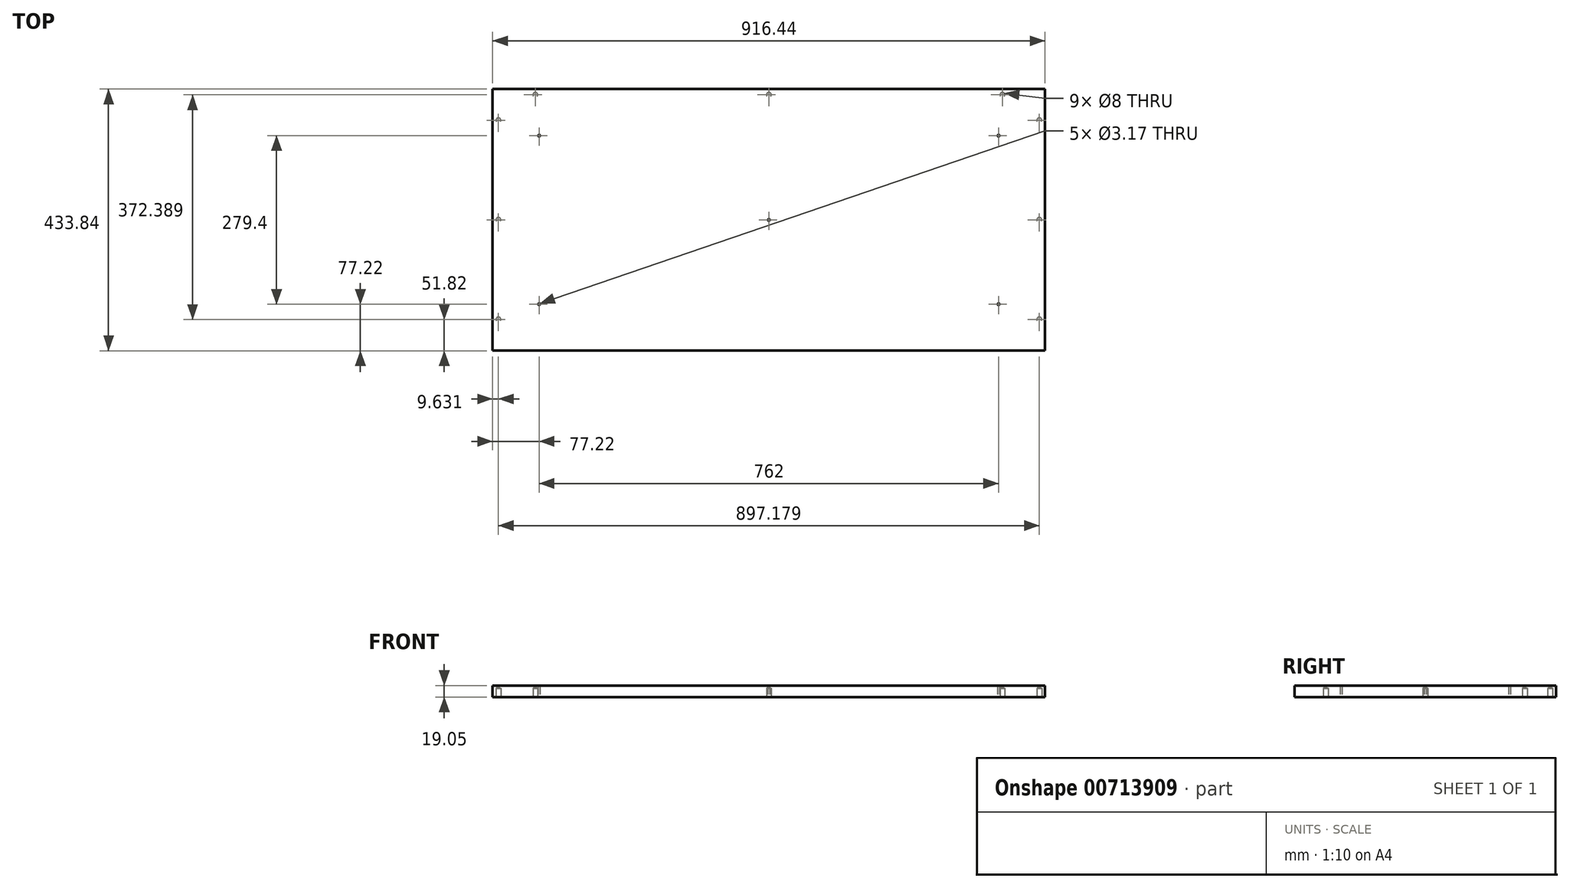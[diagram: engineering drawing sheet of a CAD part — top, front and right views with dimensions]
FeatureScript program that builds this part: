
annotation { "Feature Type Name" : "Feature", "Feature Type Description" : "" }
export const myFeature = defineFeature(function(context is Context, id is Id, definition is map)
    precondition{}
    {
        {
            var Q0;
            Q0=qCreatedBy(makeId("Top.planeOp"),FACE);
            var sketch = newSketch(context, id + "F0", { "sketchPlane" : qUnion([Q0])});
            skLineSegment(sketch, "E0.bottom", {"start": v(458.22, 216.92) * mm, "end": v(-458.22, 216.92) * mm});
            skLineSegment(sketch, "E0.top", {"start": v(458.22, -216.92) * mm, "end": v(-458.22, -216.92) * mm});
            skLineSegment(sketch, "E0.left", {"start": v(458.22, 216.92) * mm, "end": v(458.22, -216.92) * mm});
            skLineSegment(sketch, "E0.right", {"start": v(-458.22, 216.92) * mm, "end": v(-458.22, -216.92) * mm});
            skPoint(sketch, "E0.middle", {"position": v(0, 0) * mm});
            skSolve(sketch);
        }
        {
            var Q0;
            Q0=makeQuery(id+"F0.imprint","IMPRINT",FACE,{"disambiguationData":[TD([[makeQuery(id+"F0.imprint","IMPRINT",EDGE,{"derivedFrom":sQuery(id+"F0.wireOp",EDGE,"E0.bottom")}),1.0]])]});
            extrude(context, id + "F1", {"entities" : qUnion([Q0]), "depth" : 19.05 * mm, "offsetDistance" : 25.4 * mm});
        }
        {
            var Q0;
            Q0=makeQuery(id+"F1.opExtrude","CAP_FACE",FACE,{"disambiguationData":[OSD([sQuery(id+"F0.wireOp",EDGE,"E0.bottom"),sQuery(id+"F0.wireOp",EDGE,"E0.top"),sQuery(id+"F0.wireOp",EDGE,"E0.left"),sQuery(id+"F0.wireOp",EDGE,"E0.right")])],"isStart":true});
            var sketch = newSketch(context, id + "F2", { "sketchPlane" : qUnion([Q0])});
            skLineSegment(sketch, "E1", {"start": v(-458.22, 216.92) * mm, "end": v(-448.59, 216.92) * mm});
            skLineSegment(sketch, "E2", {"start": v(-448.59, 216.92) * mm, "end": v(-448.59, -216.92) * mm});
            skLineSegment(sketch, "E3", {"start": v(458.22, 216.92) * mm, "end": v(448.59, 216.92) * mm});
            skLineSegment(sketch, "E4", {"start": v(448.59, 216.92) * mm, "end": v(448.59, -216.92) * mm});
            skLineSegment(sketch, "E5", {"start": v(-448.59, -216.92) * mm, "end": v(-448.59, -207.29) * mm});
            skLineSegment(sketch, "E6", {"start": v(-448.59, -207.29) * mm, "end": v(448.59, -207.29) * mm});
            skLineSegment(sketch, "E7", {"start": v(448.59, -207.29) * mm, "end": v(458.22, -207.29) * mm});
            skLineSegment(sketch, "E8", {"start": v(-448.59, -207.29) * mm, "end": v(-458.22, -207.29) * mm});
            skLineSegment(sketch, "E9", {"start": v(-458.22, -207.29) * mm, "end": v(-387.35, -207.29) * mm});
            skLineSegment(sketch, "E10", {"start": v(458.22, -207.29) * mm, "end": v(387.35, -207.29) * mm});
            skLineSegment(sketch, "E11", {"start": v(0, -216.92) * mm, "end": v(0, -207.29) * mm});
            skLineSegment(sketch, "E12", {"start": v(-448.59, 216.92) * mm, "end": v(-448.59, 165.1) * mm});
            skLineSegment(sketch, "E13", {"start": v(448.59, 216.92) * mm, "end": v(448.59, 165.1) * mm});
            skLineSegment(sketch, "E14", {"start": v(-448.59, -216.92) * mm, "end": v(-448.59, -165.1) * mm});
            skLineSegment(sketch, "E15", {"start": v(448.59, -216.92) * mm, "end": v(448.59, -165.1) * mm});
            skLineSegment(sketch, "E16", {"start": v(-458.22, 0) * mm, "end": v(-448.59, 0) * mm});
            skLineSegment(sketch, "E17", {"start": v(458.22, 0) * mm, "end": v(448.59, 0) * mm});
            skPoint(sketch, "E18", {"position": v(-448.59, 165.1) * mm});
            skPoint(sketch, "E19", {"position": v(-448.59, 0) * mm});
            skPoint(sketch, "E20", {"position": v(-448.59, -165.1) * mm});
            skPoint(sketch, "E21", {"position": v(-387.35, -207.29) * mm});
            skPoint(sketch, "E22", {"position": v(0, -207.29) * mm});
            skPoint(sketch, "E23", {"position": v(387.35, -207.29) * mm});
            skPoint(sketch, "E24", {"position": v(448.59, -165.1) * mm});
            skPoint(sketch, "E25", {"position": v(448.59, 0) * mm});
            skPoint(sketch, "E26", {"position": v(448.59, 165.1) * mm});
            skSolve(sketch);
        }
        {
            var Q0;
            Q0=sQuery(id+"F2.wireOp",VERTEX,"E18");
            var Q1;
            Q1=sQuery(id+"F2.wireOp",VERTEX,"E19");
            var Q2;
            Q2=sQuery(id+"F2.wireOp",VERTEX,"E20");
            var Q3;
            Q3=sQuery(id+"F2.wireOp",VERTEX,"E21");
            var Q4;
            Q4=sQuery(id+"F2.wireOp",VERTEX,"E22");
            var Q5;
            Q5=sQuery(id+"F2.wireOp",VERTEX,"E23");
            var Q6;
            Q6=sQuery(id+"F2.wireOp",VERTEX,"E24");
            var Q7;
            Q7=sQuery(id+"F2.wireOp",VERTEX,"E25");
            var Q8;
            Q8=sQuery(id+"F2.wireOp",VERTEX,"E26");
            var Q9;
            Q9=makeQuery(id+"F1.opExtrude","SWEPT_BODY",BODY,{"disambiguationData":[OSD([sQuery(id+"F0.wireOp",EDGE,"E0.bottom"),sQuery(id+"F0.wireOp",EDGE,"E0.top"),sQuery(id+"F0.wireOp",EDGE,"E0.left"),sQuery(id+"F0.wireOp",EDGE,"E0.right")])]});
            hole(context, id + "F3", {"style" : HoleStyle.SIMPLE, "endStyle" : HoleEndStyle.BLIND, "holeDiameter" : 8 * mm, "majorDiameter" : 6.35 * mm, "holeDepth" : 14.22 * mm, "isTappedThrough" : true, "tappedDepth" : 12.7 * mm, "tapClearance" : 3, "startFromSketch" : true, "locations" : qUnion([Q0, Q1, Q2, Q3, Q4, Q5, Q6, Q7, Q8]), "scope" : qUnion([Q9])});
        }
        {
            var Q0;
            Q0=makeQuery(id+"F1.opExtrude","CAP_FACE",FACE,{"disambiguationData":[OSD([sQuery(id+"F0.wireOp",EDGE,"E0.bottom"),sQuery(id+"F0.wireOp",EDGE,"E0.top"),sQuery(id+"F0.wireOp",EDGE,"E0.left"),sQuery(id+"F0.wireOp",EDGE,"E0.right")])],"isStart":true});
            var sketch = newSketch(context, id + "F4", { "sketchPlane" : qUnion([Q0])});
            skLineSegment(sketch, "E27.bottom", {"start": v(381, 139.7) * mm, "end": v(-381, 139.7) * mm});
            skLineSegment(sketch, "E27.top", {"start": v(381, -139.7) * mm, "end": v(-381, -139.7) * mm});
            skLineSegment(sketch, "E27.left", {"start": v(381, 139.7) * mm, "end": v(381, -139.7) * mm});
            skLineSegment(sketch, "E27.right", {"start": v(-381, 139.7) * mm, "end": v(-381, -139.7) * mm});
            skPoint(sketch, "E27.middle", {"position": v(0, 0) * mm});
            skPoint(sketch, "E28", {"position": v(-381, 139.7) * mm});
            skPoint(sketch, "E29", {"position": v(-381, -139.7) * mm});
            skPoint(sketch, "E30", {"position": v(381, 139.7) * mm});
            skPoint(sketch, "E31", {"position": v(381, -139.7) * mm});
            skSolve(sketch);
        }
        {
            var Q0;
            Q0=sQuery(id+"F4.wireOp",VERTEX,"E28");
            var Q1;
            Q1=sQuery(id+"F4.wireOp",VERTEX,"E27.middle");
            var Q2;
            Q2=sQuery(id+"F4.wireOp",VERTEX,"E29");
            var Q3;
            Q3=sQuery(id+"F4.wireOp",VERTEX,"E31");
            var Q4;
            Q4=sQuery(id+"F4.wireOp",VERTEX,"E30");
            var Q5;
            Q5=makeQuery(id+"F1.opExtrude","SWEPT_BODY",BODY,{"disambiguationData":[OSD([sQuery(id+"F0.wireOp",EDGE,"E0.bottom"),sQuery(id+"F0.wireOp",EDGE,"E0.top"),sQuery(id+"F0.wireOp",EDGE,"E0.left"),sQuery(id+"F0.wireOp",EDGE,"E0.right")])]});
            hole(context, id + "F5", {"style" : HoleStyle.SIMPLE, "endStyle" : HoleEndStyle.BLIND, "holeDiameter" : 3.17 * mm, "majorDiameter" : 6.35 * mm, "holeDepth" : 20.32 * mm, "isTappedThrough" : true, "tappedDepth" : 12.7 * mm, "tapClearance" : 3, "startFromSketch" : true, "locations" : qUnion([Q0, Q1, Q2, Q3, Q4]), "scope" : qUnion([Q5])});
        }
    });
